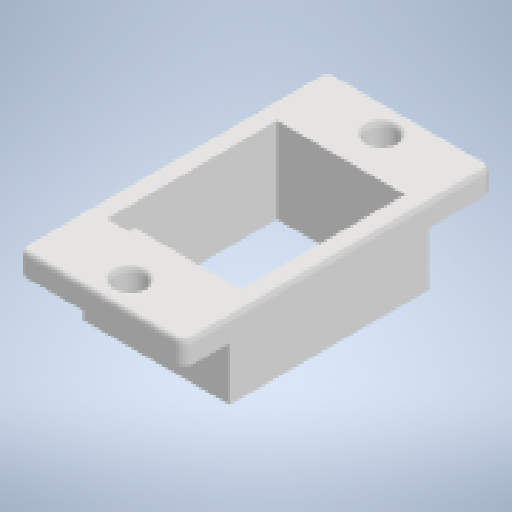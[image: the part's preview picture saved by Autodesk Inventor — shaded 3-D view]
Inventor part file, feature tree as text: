
AUTODESK INVENTOR PART (.ipt)
format: ipt  version: 2024.2 (Build 282272000, 272)  size: 285,184 bytes
history: native  units: mm
features: extrude x3, sketch x1, fillet x1
ambient origin geometry x8: Origin, YZ Plane, XZ Plane, XY Plane, X Axis, Y Axis, Z Axis, Center Point
bodies: Volumenkörper1 (feature_tree)
feature tree (5):
  sketch  "Skizze1"  dims[d0=16.8mm d1=22.8mm d2=19.5mm d3=14.7mm d4=35.5mm d5=19.12mm d6=3.2mm d7=28.9mm d8=1.0mm d9=7.3mm d10=0.0mm d11=2.5mm d12=0.0mm d13=0.5mm d14=3.2mm d15=1.0mm d16=0.0mm]
  extrude  "Extrusion1"  Depth=22.8mm
  extrude  "Extrusion2"  Depth=19.5mm
  extrude  "Extrusion3"  Depth=14.7mm
  fillet  "Rundung1"  Radius=35.5mm
